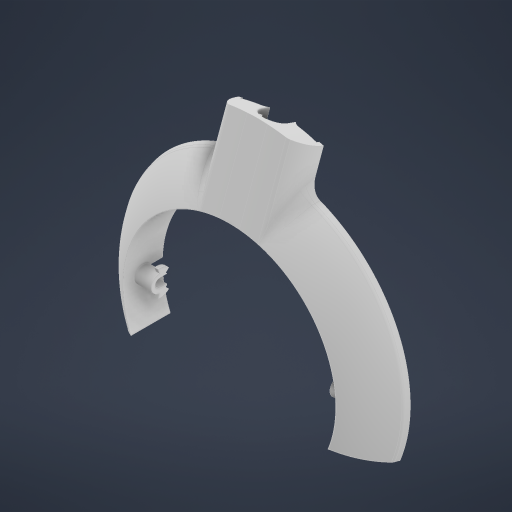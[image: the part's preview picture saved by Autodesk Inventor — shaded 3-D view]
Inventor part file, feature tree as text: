
AUTODESK INVENTOR PART (.ipt)
format: ipt  version: 2023 (Build 270158000, 158)  size: 2,184,192 bytes
history: native  units: mm
features: sketch x32, extrude x31, projected_geometry x27, fillet x14, plane x11, thicken_offset x10, reference x4, other x4, mirror x2, chamfer x1, shell x1, delete_face x1
ambient origin geometry x8: Origin, YZ Plane, XZ Plane, XY Plane, X Axis, Y Axis, Z Axis, Center Point
bodies: Body1 (feature_tree)
feature tree (138):
  extrude  "Extrusion4"  Depth=100.0mm
  chamfer  "Chamfer1"  Distance=2.0mm
  extrude  "Extrusion5"  Depth=12.0mm TaperAngle=0.0deg
  fillet  "Fillet2"  Radius=34.5mm
  fillet  "Fillet3"  Radius=80.0mm
  plane  "Work Plane4"
  extrude  "Extrusion6"  Depth=31.5mm
  plane  "Work Plane5"
  fillet  "Fillet4"  Radius=6.0mm
  extrude  "Stick"  Depth=3.0mm
  extrude  "Stickholders"  Depth=6.95mm
  plane  "Work Plane6"
  plane  "Work Plane7"
  mirror  "Mirror1"
  sketch  "Sketch12"  dims[d40=1.0mm d41=1.0mm]
  plane  "Work Plane10"
  sketch  "Sketch13"  dims[d44=9.0mm d46=4.0mm]
  extrude  "Extrusion11"  Depth=1.0mm
  extrude  "Extrusion12"  Depth=1.0mm
  plane  "Work Plane11"
  plane  "Work Plane12"
  extrude  "Extrusion13"  Depth=4.0mm
  extrude  "Extrusion15"  Depth=1.0mm
  sketch  "Sketch19"  dims[d54=90.0deg d55=15.37mm d56=0.0mm d57=8.7796mm d58=0.0mm d59=-3.5mm d60=30.534mm d61=0.0mm d65=30.0mm]
  extrude  "Extrusion16"  Depth=3.490659mm
  extrude  "Extrusion17"  Depth=15.37mm TaperAngle=0.0deg
  fillet  "Fillet5"  Radius=8.7796mm
  fillet  "Fillet6"  [1 undecoded]
  fillet  "Fillet7"  Radius=30.534mm
  shell  "Shell2"  Thickness=30.0mm
  extrude  "Extrusion19"  Depth=10.0mm TaperAngle=0.0deg
  extrude  "Extrusion23"  Depth=5.0mm
  extrude  "Extrusion24"  Depth=11.666457mm
  plane  "Work Plane14"
  mirror  "Mirror2"
  sketch  "Sketch28"  dims[d79=3.0mm d80=2.0mm]
  extrude  "Extrusion26"  Depth=10.0mm TaperAngle=0.0deg
  plane  "Work Plane15"
  extrude  "Extrusion27"  Depth=2.0mm
  sketch  "Sketch32"  dims[d96=14.5mm d97=0.0mm d99=3.0mm]
  extrude  "Extrusion29"  Depth=1.5mm
  extrude  "Extrusion30"  Depth=10.0mm TaperAngle=0.0deg
  extrude  "Extrusion31"  Depth=3.0mm
  plane  "Work Plane16"
  extrude  "Extrusion32"  Depth=0.25mm
  extrude  "Extrusion35"  Depth=0.7mm
  extrude  "Extrusion36"  Depth=0.7mm
  extrude  "Extrusion37"  Depth=0.5mm
  extrude  "Extrusion38"  Depth=1.6mm
  extrude  "Extrusion39"  Depth=1.738097mm
  extrude  "Extrusion40"  Depth=6.3mm
  extrude  "Extrusion41"  Depth=15.2824mm
  extrude  "Extrusion42"  Depth=14.5mm TaperAngle=0.0deg
  extrude  "Extrusion43"  Depth=2.0mm
  fillet  "Fillet10"  Radius=6.672053mm
  fillet  "Fillet11"  Radius=6.672122mm
  fillet  "Fillet12"  Radius=2.5mm
  extrude  "Extrusion44"  Depth=3.1mm
  fillet  "Fillet13"  Radius=1.6mm
  fillet  "Fillet14"  Radius=1.6mm
  fillet  "Fillet15"  Radius=3.334mm
  fillet  "Fillet17"  Radius=1.5mm
  delete_face  "Delete Face1"
  extrude  "Extrusion45"  Depth=1.0mm
  fillet  "Fillet18"  Radius=0.5mm
  thicken_offset  "Thicken1"
  thicken_offset  "Thicken2"
  thicken_offset  "Thicken3"
  thicken_offset  "Thicken4"
  thicken_offset  "Thicken5"
  thicken_offset  "Thicken6"
  thicken_offset  "Thicken7"
  thicken_offset  "Thicken8"
  thicken_offset  "Thicken9"
  thicken_offset  "Thicken10"
  sketch  "Sketch1"  dims[d0=75.0mm d1=100.0mm d18=2.0mm d19=0.0mm]
  sketch  "Sketch6"  dims[d20=0.5mm d21=2.0mm d22=45.0deg d23=12.0mm d24=0.0mm d25=34.5mm d26=80.0mm]
  projected_geometry  "Projected Loop2"
  sketch  "Sketch7"  dims[d27=0.1mm d28=0.0mm d29=31.5mm d30=6.0mm]
  sketch  "Sketch8"  dims[d32=0.1mm d33=0.0mm d34=3.0mm]
  sketch  "Sketch9"  dims[d36=0.5mm d37=6.95mm]
  sketch  "Sketch10"  dims[d38=6.95mm d39=1.0mm]
  plane  "Work Plane8"
  projected_geometry  "Projected Loop4"
  projected_geometry  "Projected Loop5"
  sketch  "Sketch15"  dims[d47=1.3mm d48=0.0mm d49=1.0mm]
  projected_geometry  "Projected Loop6"
  projected_geometry  "Projected Loop7"
  sketch  "Sketch18"  dims[d52=30.0mm d53=3.490659mm]
  projected_geometry  "Projected Loop11"
  projected_geometry  "Projected Loop13"
  projected_geometry  "Projected Loop14"
  sketch  "Sketch20"  dims[d66=15.0mm d67=10.0mm d68=0.0mm]
  sketch  "Sketch21"  dims[d69=5.0mm d70=5.0mm]
  projected_geometry  "Projected Loop15"
  projected_geometry  "Projected Loop16"
  sketch  "Sketch26"  dims[d71=11.666457mm d72=11.666457mm]
  sketch  "Sketch27"  dims[d73=34.25mm d74=0.0mm d75=10.0mm d76=0.0mm]
  sketch  "Sketch29"  dims[d81=5.0mm d82=1.5mm]
  projected_geometry  "Projected Loop20"
  sketch  "Sketch30"  dims[d84=32.0mm d85=10.0mm d86=0.0mm]
  projected_geometry  "Projected Loop21"
  sketch  "Sketch34"  dims[d100=0.25mm d101=0.25mm d102=0.25mm d103=0.25mm]
  projected_geometry  "Projected Loop22"
  sketch  "Sketch35"  dims[d104=14.5mm d105=0.0mm d106=0.7mm]
  sketch  "Sketch38"  dims[d107=0.7mm d108=0.7mm]
  projected_geometry  "Projected Loop33"
  projected_geometry  "Projected Loop34"
  sketch  "Sketch39"  dims[d109=0.5mm d110=0.5mm]
  reference  "Reference1"
  reference  "Reference2"
  projected_geometry  "Projected Loop35"
  sketch  "Sketch40"  dims[d111=0.5mm d112=1.6mm]
  projected_geometry  "Projected Loop36"
  reference  "Reference3"
  sketch  "Sketch41"  dims[d113=1.738097mm d114=1.738097mm]
  projected_geometry  "Projected Loop37"
  sketch  "Sketch44"  dims[d115=0.0mm d116=6.3mm]
  projected_geometry  "Projected Loop39"
  sketch  "Sketch45"  dims[d117=6.65mm d118=15.2824mm]
  projected_geometry  "Projected Loop40"
  projected_geometry  "Projected Loop41"
  sketch  "Sketch46"  dims[d119=15.282333mm d122=14.5mm d123=0.0mm]
  sketch  "Sketch47"  dims[d124=8.0mm d125=2.0mm d126=6.672053mm d127=6.672122mm d128=2.5mm d129=0.0mm]
  projected_geometry  "Projected Loop42"
  sketch  "Sketch48"  dims[d137=1.0mm d138=3.1mm d141=1.6mm d142=1.6mm]
  projected_geometry  "Projected Loop43"
  projected_geometry  "Projected Loop44"
  projected_geometry  "Projected Loop45"
  projected_geometry  "Projected Loop46"
  projected_geometry  "Projected Loop47"
  sketch  "Sketch49"  dims[d143=4.0mm d144=0.5mm d145=0.0mm d146=0.0mm d147=3.334mm d148=0.0mm d149=1.5mm d150=0.0mm]
  reference  "Reference4"
  sketch  "Sketch50"  dims[d151=-1.0mm d152=1.0mm d153=0.5mm d154=0.0mm d167=9.0mm d168=4.0mm d169=0.0mm d171=1.4mm d173=1.4mm d174=1.5mm d175=0.0mm d176=2.0mm d177=0.0mm d178=1.5mm d179=18.5mm d180=0.0mm d181=1.0mm d182=0.0mm d184=5.25mm d185=0.0mm d186=5.25mm d187=0.0mm d188=14.129mm d189=0.0mm d190=1.0mm d191=3.2mm d192=7.0mm d193=0.0mm d194=1.5mm d195=0.25mm d196=0.25mm d197=1.6mm d198=1.6mm d199=4.0mm d200=4.0mm d201=3.5mm d202=3.5mm d203=6.0mm d204=0.0mm d205=1.0mm d206=0.25mm d207=18.5mm d208=112.5deg d209=0.25mm d210=2.5mm d212=0.15mm d213=2.0mm d214=1.5mm d215=0.0mm d216=10.75mm d221=0.5mm d222=0.5mm d223=0.5mm d224=0.5mm d225=0.5mm d226=0.5mm d227=0.5mm d228=0.5mm d229=0.5mm d230=0.5mm d231=0.5mm d232=0.5mm d233=0.5mm d234=0.5mm d235=0.5mm d236=0.5mm d237=0.5mm d238=0.5mm d239=0.5mm d240=0.5mm d170=0.5mm d172=0.5mm]
  other  "<userpath>\Desktop\Model Stuff\Siberia 840\Ear Piece Holder.iam"
  other  "Ear Piece Holder.iam"
  other  "Stick:1"
  other  "Ear Back Piece:1"
note: 1 required parameter value undecoded (feature->parameter linkage not recoverable at this tier; creation-order binding heuristic only, values carry confidence <= 0.55)
